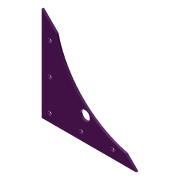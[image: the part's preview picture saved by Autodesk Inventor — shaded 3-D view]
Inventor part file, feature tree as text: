
AUTODESK INVENTOR PART (.ipt)
format: ipt  version: 2012 (Build 160160000, 160)  size: 105,472 bytes
history: native  units: in
note: dims shown in document units (in); Inventor stores cm internally (conversion verified against a paired STEP export)
features: extrude x4, sketch x4
ambient origin geometry x8: Origin, YZ Plane, XZ Plane, XY Plane, X Axis, Y Axis, Z Axis, Center Point
bodies: Solid1 (feature_tree)
feature tree (8):
  extrude  "Extrusion1"  Depth=6.0in
  extrude  "Extrusion2"  Depth=1.5in
  extrude  "Extrusion3"  Depth=0.125in TaperAngle=0.0deg
  extrude  "Extrusion5"  Depth=0.5in
  sketch  "Sketch1"  dims[d0=0.625in d1=6.0in]
  sketch  "Sketch2"  dims[d2=6.0in d3=1.5in]
  sketch  "Sketch3"  dims[d4=2.75in d5=0.125in d6=0.0in]
  sketch  "Sketch5"  dims[d7=0.25in d8=0.5in d9=0.5in d10=2.0in d11=0.25in d12=0.0in d13=2.0in d14=0.25in d15=4.0in d16=1.0in d17=0.0in d18=6.0in d23=1.0in d24=0.0in d25=6.5in d26=6.75in]
